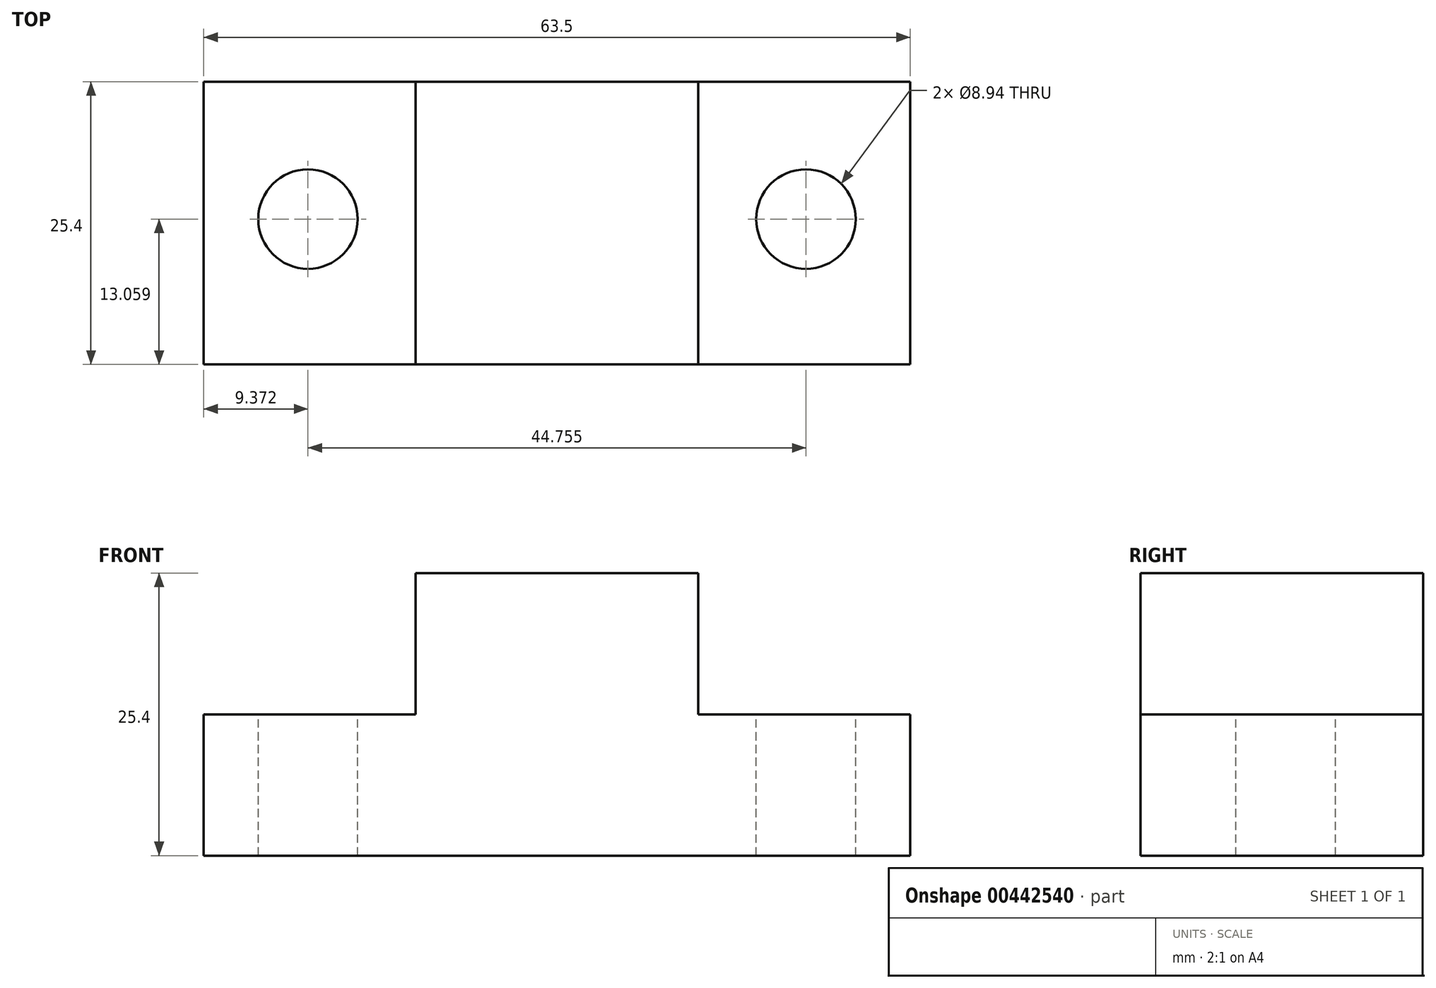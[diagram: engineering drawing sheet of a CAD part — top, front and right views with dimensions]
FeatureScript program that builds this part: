
annotation { "Feature Type Name" : "Feature", "Feature Type Description" : "" }
export const myFeature = defineFeature(function(context is Context, id is Id, definition is map)
    precondition{}
    {
        {
            var Q0;
            Q0=qCreatedBy(makeId("Front.planeOp"),FACE);
            var sketch = newSketch(context, id + "F0", { "sketchPlane" : qUnion([Q0])});
            skLineSegment(sketch, "E0", {"start": v(0, 0) * mm, "end": v(-12.7, 0) * mm});
            skLineSegment(sketch, "E1", {"start": v(-12.7, 0) * mm, "end": v(-12.7, -12.7) * mm});
            skLineSegment(sketch, "E2", {"start": v(-12.7, -12.7) * mm, "end": v(-31.75, -12.7) * mm});
            skLineSegment(sketch, "E3", {"start": v(-31.75, -12.7) * mm, "end": v(-31.75, -25.4) * mm});
            skLineSegment(sketch, "E4", {"start": v(-31.75, -25.4) * mm, "end": v(0, -25.4) * mm});
            skLineSegment(sketch, "E5", {"start": v(0, -25.4) * mm, "end": v(0, 0) * mm});
            skSolve(sketch);
        }
        {
            var Q0;
            Q0=makeQuery(id+"F0.imprint","IMPRINT",FACE,{"disambiguationData":[TD([[makeQuery(id+"F0.imprint","IMPRINT",EDGE,{"derivedFrom":sQuery(id+"F0.wireOp",EDGE,"E0")}),1.0]])]});
            extrude(context, id + "F1", {"entities" : qUnion([Q0]), "depth" : 25.4 * mm});
        }
        {
            var Q0;
            Q0=makeQuery(id+"F1.opExtrude","SWEPT_FACE",FACE,{"disambiguationData":[OSD([sQuery(id+"F0.wireOp",EDGE,"E2")])]});
            var sketch = newSketch(context, id + "F2", { "sketchPlane" : qUnion([Q0])});
            skCircle(sketch, "E6", {"center": v(-22.38, -12.34) * mm, "radius": 4.47 * mm});
            skSolve(sketch);
        }
        {
            var Q0;
            Q0=makeQuery(id+"F2.imprint","IMPRINT",FACE,{"disambiguationData":[TD([[makeQuery(id+"F2.imprint","IMPRINT",EDGE,{"derivedFrom":sQuery(id+"F2.wireOp",EDGE,"E6")}),1.0]])]});
            extrude(context, id + "F3", {"entities" : qUnion([Q0]), "operationType" : NewBodyOperationType.REMOVE, "oppositeDirection" : true, "depth" : 25.4 * mm});
        }
        {
            var Q0;
            Q0=makeQuery(id+"F1.opExtrude","SWEPT_BODY",BODY,{"disambiguationData":[OSD([sQuery(id+"F0.wireOp",EDGE,"E0"),sQuery(id+"F0.wireOp",EDGE,"E1"),sQuery(id+"F0.wireOp",EDGE,"E2"),sQuery(id+"F0.wireOp",EDGE,"E3"),sQuery(id+"F0.wireOp",EDGE,"E4"),sQuery(id+"F0.wireOp",EDGE,"E5")])]});
            var Q1;
            Q1=qCreatedBy(makeId("Right.planeOp"),FACE);
            mirror(context, id + "F4", {"operationType" : NewBodyOperationType.ADD, "entities" : qUnion([Q0]), "mirrorPlane" : qUnion([Q1])});
        }
    });
